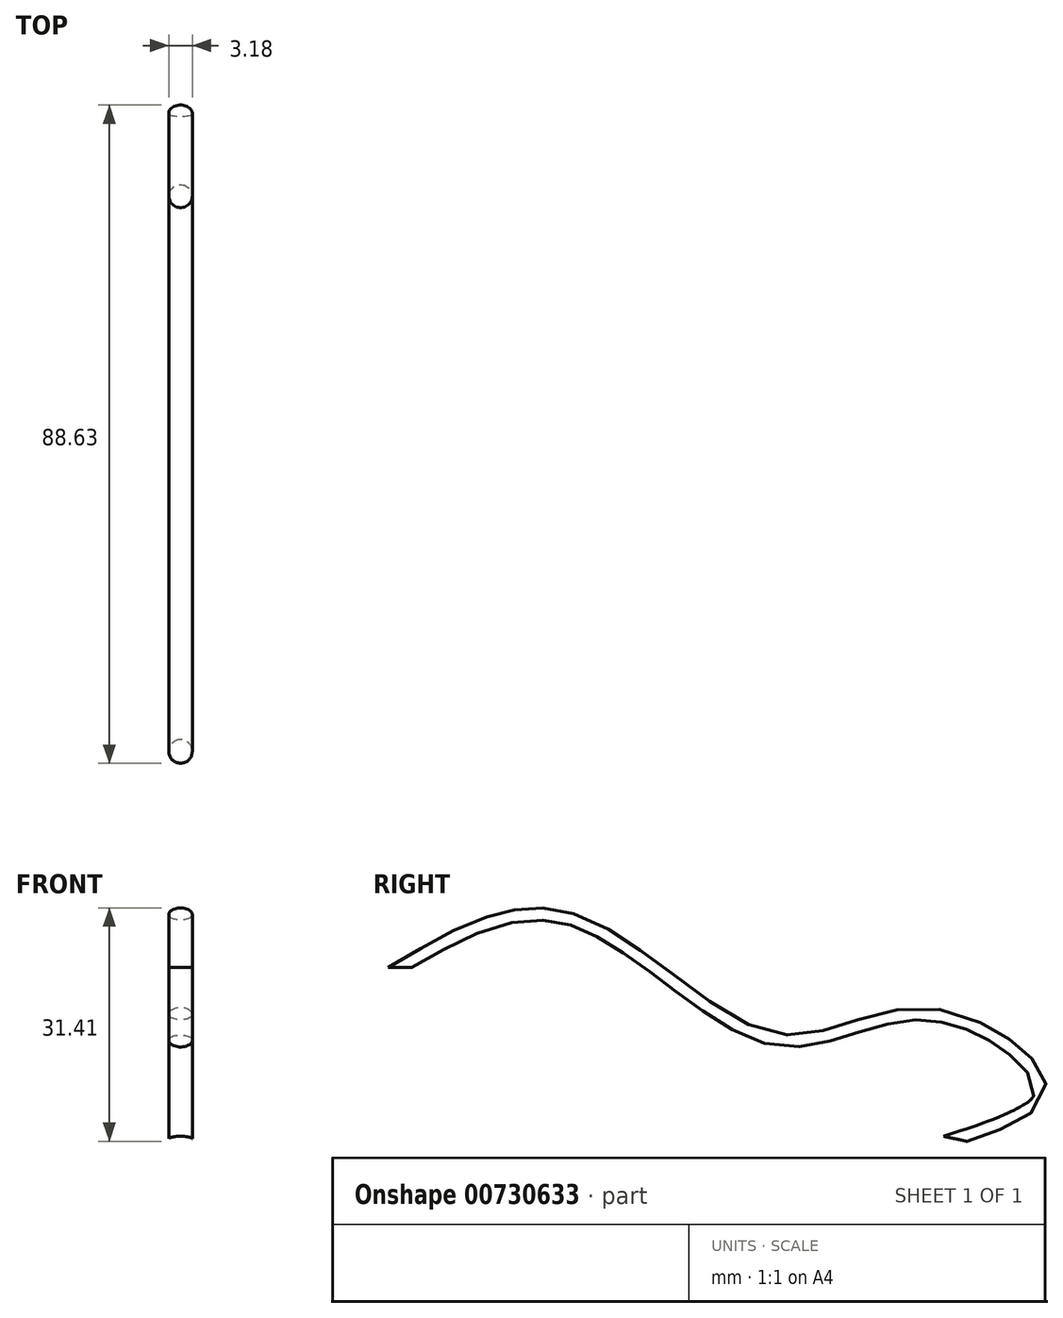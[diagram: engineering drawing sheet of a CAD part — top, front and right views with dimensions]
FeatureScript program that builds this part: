
annotation { "Feature Type Name" : "Feature", "Feature Type Description" : "" }
export const myFeature = defineFeature(function(context is Context, id is Id, definition is map)
    precondition{}
    {
        {
            var Q0;
            Q0=qCreatedBy(makeId("Right.planeOp"),FACE);
            var sketch = newSketch(context, id + "F0", { "sketchPlane" : qUnion([Q0])});
            skFitSpline(sketch, "E0", {"points": [v(0, 0) * mm, v(22.9, 6.5) * mm, v(50.23, -9.6) * mm, v(71.26, -6.36) * mm, v(85.97, -16.14) * mm, v(74.76, -23.08) * mm], "startDerivative": vector(106, 62.31) * mm, "endDerivative": vector(-107.1, -35.41) * mm});
            skSolve(sketch);
        }
        {
            var Q0;
            Q0=qCreatedBy(makeId("Top.planeOp"),FACE);
            var sketch = newSketch(context, id + "F1", { "sketchPlane" : qUnion([Q0])});
            skCircle(sketch, "E1", {"center": v(0, 0) * mm, "radius": 1.59 * mm});
            skSolve(sketch);
        }
        {
            var Q0;
            Q0=makeQuery(id+"F1.imprint","IMPRINT",FACE,{"disambiguationData":[TD([[makeQuery(id+"F1.imprint","IMPRINT",EDGE,{"derivedFrom":sQuery(id+"F1.wireOp",EDGE,"E1")}),1.0]])]});
            var Q1;
            Q1=sQuery(id+"F0.wireOp",EDGE,"E0");
            sweep(context, id + "F2", {"profiles" : qUnion([Q0]), "path" : qUnion([Q1])});
        }
    });
